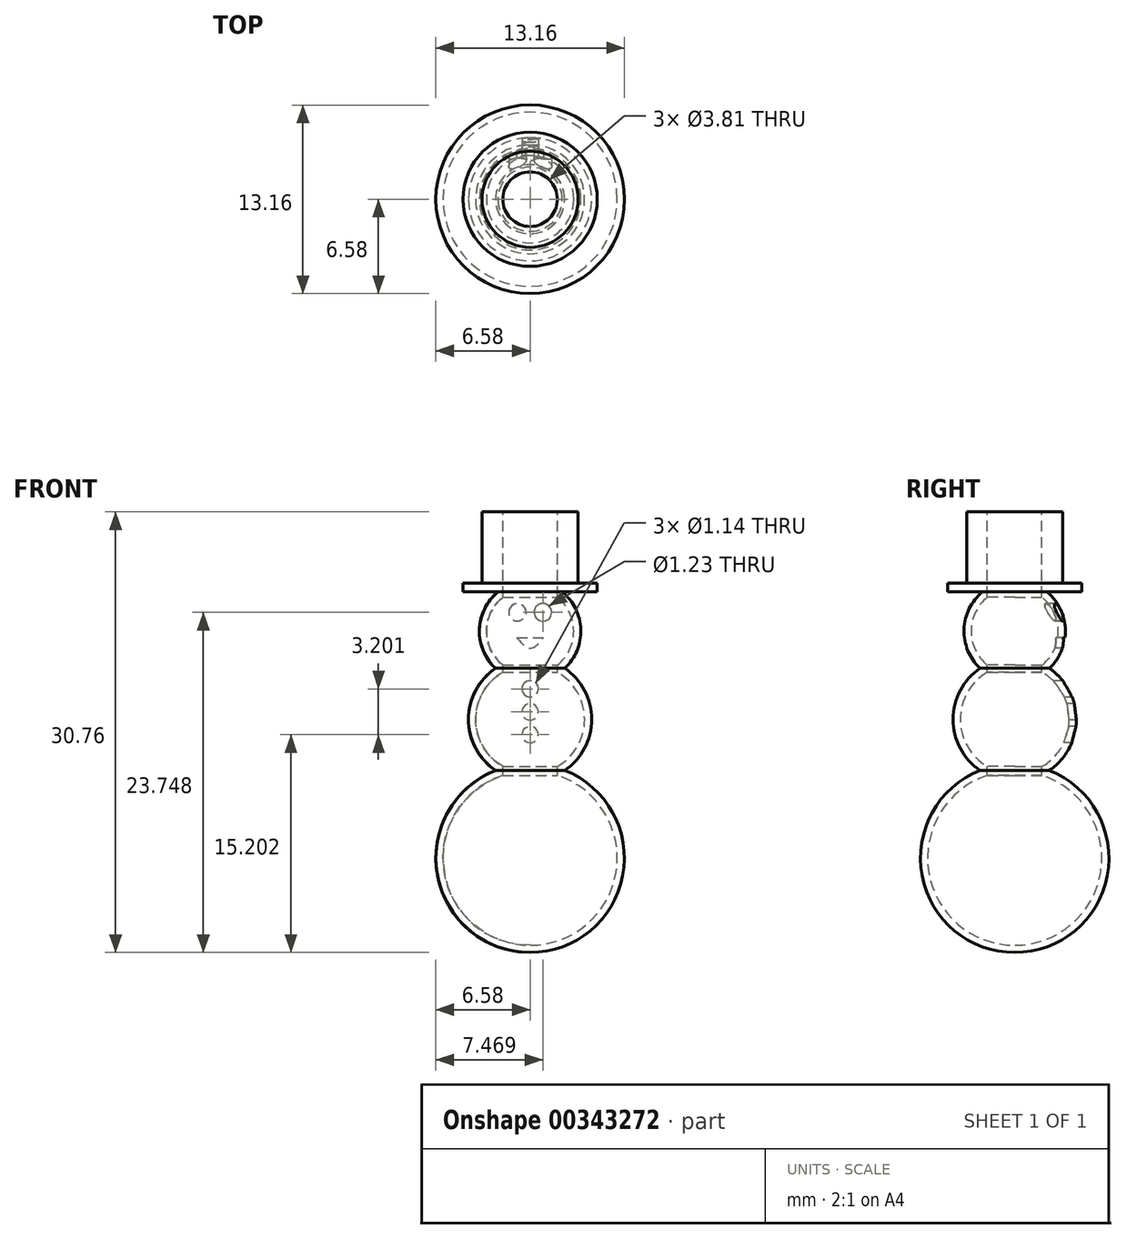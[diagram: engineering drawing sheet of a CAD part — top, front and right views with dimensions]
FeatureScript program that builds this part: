
annotation { "Feature Type Name" : "Feature", "Feature Type Description" : "" }
export const myFeature = defineFeature(function(context is Context, id is Id, definition is map)
    precondition{}
    {
        {
            var Q0;
            Q0=qCreatedBy(makeId("Top.planeOp"),FACE);
            var sketch = newSketch(context, id + "F0", { "sketchPlane" : qUnion([Q0])});
            skCircle(sketch, "E0", {"center": v(0, 0) * mm, "radius": 3.36 * mm});
            skSolve(sketch);
        }
        {
            var Q0;
            Q0=makeQuery(id+"F0.imprint","IMPRINT",FACE,{"disambiguationData":[TD([[makeQuery(id+"F0.imprint","IMPRINT",EDGE,{"derivedFrom":sQuery(id+"F0.wireOp",EDGE,"E0")}),1.0]])]});
            extrude(context, id + "F1", {"entities" : qUnion([Q0]), "depth" : 5.6 * mm});
        }
        {
            var Q0;
            Q0=qCreatedBy(makeId("Top.planeOp"),FACE);
            var sketch = newSketch(context, id + "F2", { "sketchPlane" : qUnion([Q0])});
            skCircle(sketch, "E1", {"center": v(0, 0) * mm, "radius": 4.69 * mm});
            skSolve(sketch);
        }
        {
            var Q0;
            Q0=makeQuery(id+"F2.imprint","IMPRINT",FACE,{"disambiguationData":[TD([[makeQuery(id+"F2.imprint","IMPRINT",EDGE,{"derivedFrom":sQuery(id+"F2.wireOp",EDGE,"E1")}),1.0]])]});
            extrude(context, id + "F3", {"entities" : qUnion([Q0]), "operationType" : NewBodyOperationType.ADD, "depth" : 0.6 * mm});
        }
        {
            var Q0;
            Q0=qCreatedBy(makeId("Front.planeOp"),FACE);
            var sketch = newSketch(context, id + "F4", { "sketchPlane" : qUnion([Q0])});
            skLineSegment(sketch, "E2", {"start": v(0, 0.8) * mm, "end": v(0, -6.28) * mm});
            skArc(sketch, "E3", {"start": v(0, -6.28) * mm, "mid": v(3.54, -2.74) * mm, "end": v(0, 0.8) * mm});
            skSolve(sketch);
        }
        {
            var Q0;
            Q0 = qSketchRegion(id + "F4", true);
            var Q1;
            Q1=sQuery(id+"F4.wireOp",EDGE,"E2");
            revolve(context, id + "F5", {"operationType" : NewBodyOperationType.ADD, "entities" : qUnion([Q0]), "axis" : qUnion([Q1]), "revolveType" : RevolveType.FULL});
        }
        {
            var Q0;
            Q0=makeQuery(id+"F1.opExtrude","CAP_FACE",FACE,{"disambiguationData":[OSD([sQuery(id+"F0.wireOp",EDGE,"E0")])],"isStart":false});
            var sketch = newSketch(context, id + "F6", { "sketchPlane" : qUnion([Q0])});
            skCircle(sketch, "E4", {"center": v(0, 0) * mm, "radius": 1.9 * mm});
            skSolve(sketch);
        }
        {
            var Q0;
            Q0=qCreatedBy(makeId("Front.planeOp"),FACE);
            var sketch = newSketch(context, id + "F7", { "sketchPlane" : qUnion([Q0])});
            skLineSegment(sketch, "E5", {"start": v(0, -4.6) * mm, "end": v(0, -13.2) * mm});
            skArc(sketch, "E6", {"start": v(0, -13.2) * mm, "mid": v(4.3, -8.9) * mm, "end": v(0, -4.6) * mm});
            skSolve(sketch);
        }
        {
            var Q0;
            Q0=makeQuery(id+"F6.imprint","IMPRINT",FACE,{"disambiguationData":[TD([[makeQuery(id+"F6.imprint","IMPRINT",EDGE,{"derivedFrom":sQuery(id+"F6.wireOp",EDGE,"E4")}),1.0]])]});
            extrude(context, id + "F8", {"entities" : qUnion([Q0]), "operationType" : NewBodyOperationType.REMOVE, "oppositeDirection" : true, "depth" : 0.2 * mm});
        }
        {
            var Q0;
            Q0 = qSketchRegion(id + "F7", true);
            var Q1;
            Q1=sQuery(id+"F7.wireOp",EDGE,"E5");
            revolve(context, id + "F9", {"operationType" : NewBodyOperationType.ADD, "entities" : qUnion([Q0]), "axis" : qUnion([Q1]), "revolveType" : RevolveType.FULL});
        }
        {
            var Q0;
            Q0=qCreatedBy(makeId("Front.planeOp"),FACE);
            var sketch = newSketch(context, id + "F10", { "sketchPlane" : qUnion([Q0])});
            skLineSegment(sketch, "E7", {"start": v(0, -12) * mm, "end": v(0, -25.17) * mm});
            skArc(sketch, "E8", {"start": v(0, -25.17) * mm, "mid": v(6.58, -18.59) * mm, "end": v(0, -12) * mm});
            skSolve(sketch);
        }
        {
            var Q0;
            Q0 = qSketchRegion(id + "F10", true);
            var Q1;
            Q1=sQuery(id+"F10.wireOp",EDGE,"E7");
            revolve(context, id + "F11", {"operationType" : NewBodyOperationType.ADD, "entities" : qUnion([Q0]), "axis" : qUnion([Q1]), "revolveType" : RevolveType.FULL});
        }
        {
            var Q0;
            Q0=makeQuery(id+"F8.boolean.opBoolean","COPY",FACE,{"derivedFrom":makeQuery(id+"F8.opExtrude","CAP_FACE",FACE,{"disambiguationData":[OSD([sQuery(id+"F6.wireOp",EDGE,"E4")])],"isStart":false})});
            shell(context, id + "F12", {"entities" : qUnion([Q0]), "thickness" : .5 * mm});
        }
        {
            var Q0;
            Q0=makeQuery(id+"F8.boolean.opBoolean","COPY",FACE,{"derivedFrom":makeQuery(id+"F8.opExtrude","CAP_FACE",FACE,{"disambiguationData":[OSD([sQuery(id+"F6.wireOp",EDGE,"E4")])],"isStart":false})});
            extrude(context, id + "F13", {"entities" : qUnion([Q0]), "operationType" : NewBodyOperationType.REMOVE, "oppositeDirection" : true, "depth" : 27.94 * mm});
        }
        {
            var Q0;
            Q0=qCreatedBy(makeId("Front.planeOp"),FACE);
            var sketch = newSketch(context, id + "F14", { "sketchPlane" : qUnion([Q0])});
            skCircle(sketch, "E9", {"center": v(0, -6.77) * mm, "radius": 0.57 * mm});
            skCircle(sketch, "E10", {"center": v(0, -8.37) * mm, "radius": 0.57 * mm});
            skCircle(sketch, "E11", {"center": v(0, -9.97) * mm, "radius": 0.57 * mm});
            skSolve(sketch);
        }
        {
            var Q0;
            Q0 = qSketchRegion(id + "F14", true);
            extrude(context, id + "F15", {"entities" : qUnion([Q0]), "operationType" : NewBodyOperationType.REMOVE, "oppositeDirection" : true, "depth" : 14.48 * mm});
        }
        {
            var Q0;
            Q0=qCreatedBy(makeId("Front.planeOp"),FACE);
            var sketch = newSketch(context, id + "F16", { "sketchPlane" : qUnion([Q0])});
            skCircle(sketch, "E12", {"center": v(0.89, -1.42) * mm, "radius": 0.62 * mm});
            skCircle(sketch, "E13", {"center": v(-0.89, -1.42) * mm, "radius": 0.6 * mm});
            skSolve(sketch);
        }
        {
            var Q0;
            Q0 = qSketchRegion(id + "F16", true);
            extrude(context, id + "F17", {"entities" : qUnion([Q0]), "operationType" : NewBodyOperationType.REMOVE, "oppositeDirection" : true, "depth" : 25.4 * mm});
        }
        {
            var Q0;
            Q0=qCreatedBy(makeId("Front.planeOp"),FACE);
            var sketch = newSketch(context, id + "F18", { "sketchPlane" : qUnion([Q0])});
            skLineSegment(sketch, "E14", {"start": v(-0.94, -3.19) * mm, "end": v(0.93, -3.19) * mm});
            skFitSpline(sketch, "E15", {"points": [v(-0.94, -3.19) * mm, v(0, -3.93) * mm, v(0.93, -3.19) * mm], "startDerivative": vector(1.87, -2.21) * mm, "endDerivative": vector(1.87, 2.21) * mm});
            skSolve(sketch);
        }
        {
            var Q0;
            Q0 = qSketchRegion(id + "F18", true);
            extrude(context, id + "F19", {"entities" : qUnion([Q0]), "operationType" : NewBodyOperationType.REMOVE, "oppositeDirection" : true, "depth" : 25.4 * mm});
        }
    });
